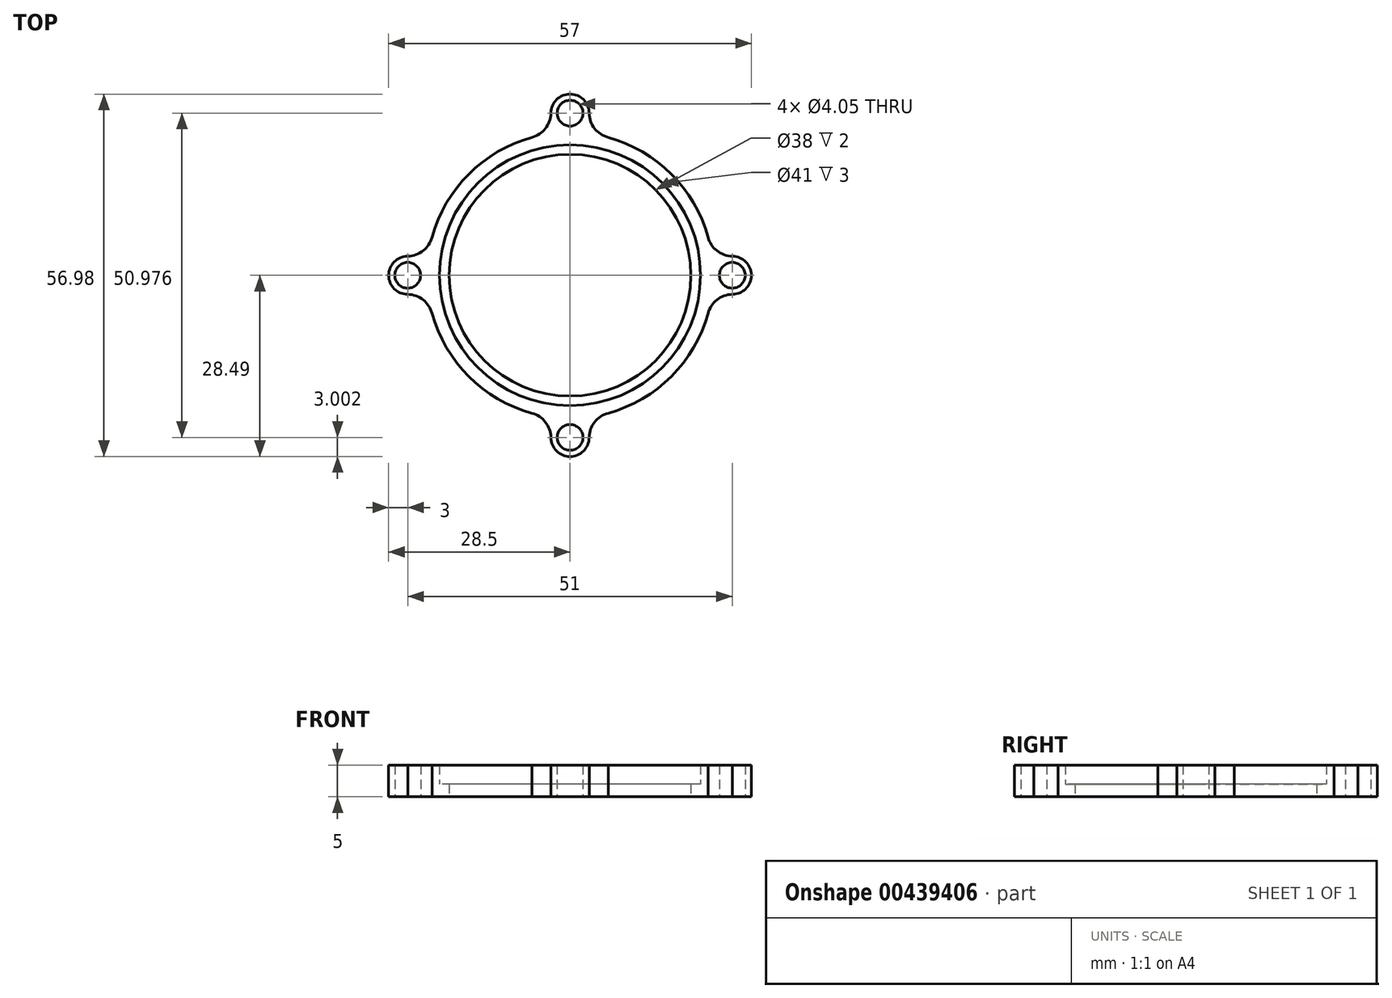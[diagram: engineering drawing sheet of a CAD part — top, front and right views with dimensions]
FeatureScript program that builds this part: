
annotation { "Feature Type Name" : "Feature", "Feature Type Description" : "" }
export const myFeature = defineFeature(function(context is Context, id is Id, definition is map)
    precondition{}
    {
        {
            var Q0;
            Q0=qCreatedBy(makeId("Top.planeOp"),FACE);
            var sketch = newSketch(context, id + "F0", { "sketchPlane" : qUnion([Q0])});
            skCircle(sketch, "E0", {"center": v(0, 0) * mm, "radius": 19 * mm});
            skCircle(sketch, "E1", {"center": v(0, 0) * mm, "radius": 20.5 * mm});
            skArc(sketch, "E2", {"start": v(-25.5, 3) * mm, "mid": v(-28.5, 0) * mm, "end": v(-25.5, -3) * mm});
            skCircle(sketch, "E3", {"center": v(-25.5, 0) * mm, "radius": 2.02 * mm});
            skArc(sketch, "E4.MirrorC", {"start": v(25.5, 3) * mm, "mid": v(28.5, 0) * mm, "end": v(25.5, -3) * mm});
            skCircle(sketch, "E5.MirrorC", {"center": v(25.5, 0) * mm, "radius": 2.02 * mm});
            skPoint(sketch, "E6.center", {"position": v(0, -0.01) * mm});
            skArc(sketch, "E7", {"start": v(3, 25.49) * mm, "mid": v(0, 28.49) * mm, "end": v(-3, 25.49) * mm});
            skCircle(sketch, "E8", {"center": v(0, 25.49) * mm, "radius": 2.02 * mm});
            skArc(sketch, "E9", {"start": v(-3, -25.49) * mm, "mid": v(0, -28.51) * mm, "end": v(3, -25.49) * mm});
            skArc(sketch, "E10", {"start": v(-25.5, 3) * mm, "mid": v(-23.09, 3.86) * mm, "end": v(-21.69, 6) * mm});
            skArc(sketch, "E11.MirrorCS", {"start": v(-25.5, -3) * mm, "mid": v(-23.09, -3.86) * mm, "end": v(-21.69, -6) * mm});
            skArc(sketch, "E12", {"start": v(3, 25.49) * mm, "mid": v(3.86, 23.08) * mm, "end": v(6, 21.69) * mm});
            skArc(sketch, "E13.MirrorCS", {"start": v(-3, 25.49) * mm, "mid": v(-3.86, 23.08) * mm, "end": v(-6, 21.69) * mm});
            skArc(sketch, "E14", {"start": v(21.69, 6) * mm, "mid": v(23.09, 3.86) * mm, "end": v(25.5, 3) * mm});
            skArc(sketch, "E15.MirrorCS", {"start": v(21.69, -6) * mm, "mid": v(23.09, -3.86) * mm, "end": v(25.5, -3) * mm});
            skArc(sketch, "E16", {"start": v(-3, -25.49) * mm, "mid": v(-3.86, -23.08) * mm, "end": v(-6, -21.69) * mm});
            skArc(sketch, "E17.MirrorCS", {"start": v(3, -25.49) * mm, "mid": v(3.86, -23.08) * mm, "end": v(6, -21.69) * mm});
            skCircle(sketch, "E18", {"center": v(0, -25.49) * mm, "radius": 2.02 * mm});
            skArc(sketch, "E19.trimOffspring", {"start": v(5.89, -21.72) * mm, "mid": v(15.9, -15.91) * mm, "end": v(21.72, -5.89) * mm});
            skArc(sketch, "E20.trimOffspring", {"start": v(3, -25.49) * mm, "mid": v(0, -28.49) * mm, "end": v(-3, -25.49) * mm});
            skArc(sketch, "E21.trimOffspring", {"start": v(21.72, 5.89) * mm, "mid": v(15.9, 15.91) * mm, "end": v(5.89, 21.72) * mm});
            skArc(sketch, "E22.trimOffspring", {"start": v(-5.89, 21.72) * mm, "mid": v(-15.9, 15.91) * mm, "end": v(-21.72, 5.89) * mm});
            skArc(sketch, "E23.trimOffspring", {"start": v(-21.72, -5.89) * mm, "mid": v(-15.9, -15.91) * mm, "end": v(-5.89, -21.72) * mm});
            skSolve(sketch);
        }
        {
            var Q0;
            Q0=makeQuery(id+"F0.imprint","IMPRINT",FACE,{"disambiguationData":[TD([[makeQuery(id+"F0.imprint","IMPRINT",EDGE,{"derivedFrom":sQuery(id+"F0.wireOp",EDGE,"E0")}),-1.0]])]});
            var Q1;
            Q1=sQuery(id+"F0.wireOp",EDGE,"E1");
            extrude(context, id + "F1", {"entities" : qUnion([Q0]), "surfaceEntities" : qUnion([Q1]), "depth" : 2 * mm});
        }
        {
            var Q0;
            Q0=makeQuery(id+"F0.imprint","IMPRINT",FACE,{"disambiguationData":[TD([[makeQuery(id+"F0.imprint","IMPRINT",EDGE,{"derivedFrom":sQuery(id+"F0.wireOp",EDGE,"E1")}),-1.0]])]});
            extrude(context, id + "F2", {"entities" : qUnion([Q0]), "operationType" : NewBodyOperationType.ADD, "depth" : 5 * mm});
        }
    });
